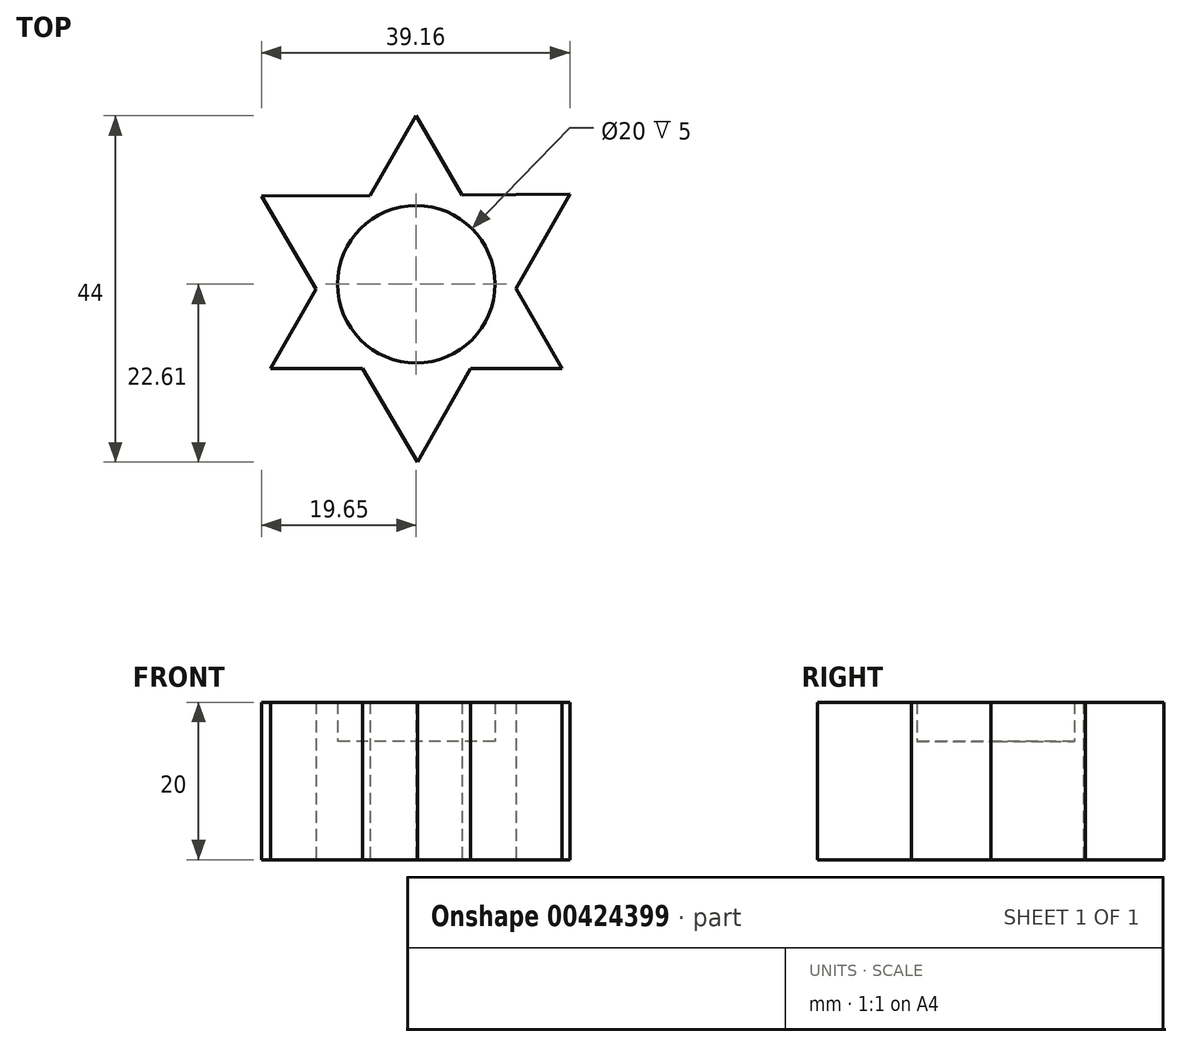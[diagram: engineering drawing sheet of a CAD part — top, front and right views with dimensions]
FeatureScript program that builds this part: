
annotation { "Feature Type Name" : "Feature", "Feature Type Description" : "" }
export const myFeature = defineFeature(function(context is Context, id is Id, definition is map)
    precondition{}
    {
        {
            var Q0;
            Q0=qCreatedBy(makeId("Top.planeOp"),FACE);
            var sketch = newSketch(context, id + "F0", { "sketchPlane" : qUnion([Q0])});
            skCircle(sketch, "E0.cCircle", {"center": v(0, 0) * mm, "radius": 21.4 * mm, "construction": true});
            skLineSegment(sketch, "E0.0", {"start": v(0, 21.4) * mm, "end": v(18.53, -10.7) * mm});
            skLineSegment(sketch, "E0.1", {"start": v(18.53, -10.7) * mm, "end": v(-18.53, -10.7) * mm});
            skLineSegment(sketch, "E0.2", {"start": v(-18.53, -10.7) * mm, "end": v(0, 21.4) * mm});
            skCircle(sketch, "E1.cCircle", {"center": v(0, 0) * mm, "radius": 22.6 * mm, "construction": true});
            skLineSegment(sketch, "E1.0", {"start": v(19.5, 11.42) * mm, "end": v(0.14, -22.6) * mm});
            skLineSegment(sketch, "E1.1", {"start": v(0.14, -22.6) * mm, "end": v(-19.65, 11.18) * mm});
            skLineSegment(sketch, "E1.2", {"start": v(-19.65, 11.18) * mm, "end": v(19.5, 11.42) * mm});
            skLineSegment(sketch, "E2", {"start": v(0, 21.4) * mm, "end": v(0.14, -22.6) * mm});
            skSolve(sketch);
        }
        {
            var Q0;
            {var subQ0=sQuery(id+"F0.wireOp",EDGE,"E1.1");var subQ1=sQuery(id+"F0.wireOp",EDGE,"E0.2");var subQ2=makeQuery(id+"F0.imprint","INTERSECT",VERTEX,{"derivedFrom":[subQ1,subQ0]});Q0=makeQuery(id+"F0.imprint","IMPRINT",FACE,{"disambiguationData":[TD([[makeQuery(id+"F0.imprint","IMPRINT",EDGE,{"disambiguationData":[TD([[subQ2,-1.0]])],"derivedFrom":subQ1}),1.0]])]});}
            var Q1;
            {var subQ5=sQuery(id+"F0.wireOp",EDGE,"E1.1");var subQ6=sQuery(id+"F0.wireOp",EDGE,"E0.1");var subQ7=makeQuery(id+"F0.imprint","INTERSECT",VERTEX,{"derivedFrom":[subQ6,subQ5]});Q1=makeQuery(id+"F0.imprint","IMPRINT",FACE,{"disambiguationData":[TD([[makeQuery(id+"F0.imprint","IMPRINT",EDGE,{"disambiguationData":[TD([[subQ7,1.0]])],"derivedFrom":subQ6}),-1.0]])]});}
            var Q2;
            {var subQ1=sQuery(id+"F0.wireOp",EDGE,"E0.2");var subQ3=sQuery(id+"F0.wireOp",EDGE,"E1.2");var subQ4=makeQuery(id+"F0.imprint","INTERSECT",VERTEX,{"derivedFrom":[subQ1,subQ3]});Q2=makeQuery(id+"F0.imprint","IMPRINT",FACE,{"disambiguationData":[TD([[makeQuery(id+"F0.imprint","IMPRINT",EDGE,{"disambiguationData":[TD([[subQ4,-1.0]])],"derivedFrom":subQ3}),1.0]])]});}
            var Q3;
            {var subQ1=sQuery(id+"F0.wireOp",EDGE,"E0.0");var subQ3=sQuery(id+"F0.wireOp",EDGE,"E1.2");var subQ4=makeQuery(id+"F0.imprint","INTERSECT",VERTEX,{"derivedFrom":[subQ1,subQ3]});Q3=makeQuery(id+"F0.imprint","IMPRINT",FACE,{"disambiguationData":[TD([[makeQuery(id+"F0.imprint","IMPRINT",EDGE,{"disambiguationData":[TD([[subQ4,1.0]])],"derivedFrom":subQ3}),1.0]])]});}
            var Q4;
            {var subQ0=sQuery(id+"F0.wireOp",EDGE,"E1.2");var subQ1=sQuery(id+"F0.wireOp",EDGE,"E0.0");var subQ2=makeQuery(id+"F0.imprint","INTERSECT",VERTEX,{"derivedFrom":[subQ1,subQ0]});Q4=makeQuery(id+"F0.imprint","IMPRINT",FACE,{"disambiguationData":[TD([[makeQuery(id+"F0.imprint","IMPRINT",EDGE,{"disambiguationData":[TD([[subQ2,-1.0]])],"derivedFrom":subQ1}),-1.0]])]});}
            var Q5;
            {var subQ0=sQuery(id+"F0.wireOp",EDGE,"E1.2");var subQ1=sQuery(id+"F0.wireOp",EDGE,"E0.0");var subQ2=makeQuery(id+"F0.imprint","INTERSECT",VERTEX,{"derivedFrom":[subQ1,subQ0]});Q5=makeQuery(id+"F0.imprint","IMPRINT",FACE,{"disambiguationData":[TD([[makeQuery(id+"F0.imprint","IMPRINT",EDGE,{"disambiguationData":[TD([[subQ2,-1.0]])],"derivedFrom":subQ1}),1.0]])]});}
            var Q6;
            {var subQ0=sQuery(id+"F0.wireOp",EDGE,"E0.1");var subQ1=sQuery(id+"F0.wireOp",EDGE,"E0.0");var subQ2=makeQuery(id+"F0.imprint","INTERSECT",VERTEX,{"derivedFrom":[subQ1,subQ0]});Q6=makeQuery(id+"F0.imprint","IMPRINT",FACE,{"disambiguationData":[TD([[makeQuery(id+"F0.imprint","IMPRINT",EDGE,{"disambiguationData":[TD([[subQ2,1.0]])],"derivedFrom":subQ1}),-1.0]])]});}
            var Q7;
            {var subQ0=sQuery(id+"F0.wireOp",EDGE,"E1.1");var subQ1=sQuery(id+"F0.wireOp",EDGE,"E0.1");var subQ2=makeQuery(id+"F0.imprint","INTERSECT",VERTEX,{"derivedFrom":[subQ1,subQ0]});Q7=makeQuery(id+"F0.imprint","IMPRINT",FACE,{"disambiguationData":[TD([[makeQuery(id+"F0.imprint","IMPRINT",EDGE,{"disambiguationData":[TD([[subQ2,1.0]])],"derivedFrom":subQ1}),1.0]])]});}
            var Q8;
            {var subQ0=sQuery(id+"F0.wireOp",EDGE,"E1.0");var subQ1=sQuery(id+"F0.wireOp",EDGE,"E0.1");var subQ2=makeQuery(id+"F0.imprint","INTERSECT",VERTEX,{"derivedFrom":[subQ1,subQ0]});Q8=makeQuery(id+"F0.imprint","IMPRINT",FACE,{"disambiguationData":[TD([[makeQuery(id+"F0.imprint","IMPRINT",EDGE,{"disambiguationData":[TD([[subQ2,-1.0]])],"derivedFrom":subQ1}),1.0]])]});}
            var Q9;
            {var subQ0=sQuery(id+"F0.wireOp",EDGE,"E0.2");var subQ1=sQuery(id+"F0.wireOp",EDGE,"E0.1");var subQ2=makeQuery(id+"F0.imprint","INTERSECT",VERTEX,{"derivedFrom":[subQ1,subQ0]});Q9=makeQuery(id+"F0.imprint","IMPRINT",FACE,{"disambiguationData":[TD([[makeQuery(id+"F0.imprint","IMPRINT",EDGE,{"disambiguationData":[TD([[subQ2,1.0]])],"derivedFrom":subQ1}),-1.0]])]});}
            extrude(context, id + "F1", {"entities" : qUnion([Q0, Q1, Q2, Q3, Q4, Q5, Q6, Q7, Q8, Q9]), "depth" : 15 * mm, "offsetDistance" : 25 * mm});
        }
        {
            var Q0;
            Q0=makeQuery(id+"F1.opExtrude","CAP_FACE",FACE,{"disambiguationData":[OSD([sQuery(id+"F0.wireOp",EDGE,"E0.0"),sQuery(id+"F0.wireOp",EDGE,"E0.1"),sQuery(id+"F0.wireOp",EDGE,"E0.2"),sQuery(id+"F0.wireOp",EDGE,"E1.0"),sQuery(id+"F0.wireOp",EDGE,"E1.1"),sQuery(id+"F0.wireOp",EDGE,"E1.2")])],"isStart":false});
            var sketch = newSketch(context, id + "F2", { "sketchPlane" : qUnion([Q0])});
            skCircle(sketch, "E3", {"center": v(0, 0) * mm, "radius": 10 * mm});
            skLineSegment(sketch, "E4", {"start": v(0, 0) * mm, "end": v(10, 0) * mm});
            skSolve(sketch);
        }
        {
            var Q0;
            Q0=makeQuery(id+"F2.imprint","IMPRINT",FACE,{"disambiguationData":[TD([[makeQuery(id+"F2.imprint","IMPRINT",EDGE,{"derivedFrom":sQuery(id+"F2.wireOp",EDGE,"E3")}),-1.0]])]});
            extrude(context, id + "F3", {"entities" : qUnion([Q0]), "operationType" : NewBodyOperationType.ADD, "depth" : 5 * mm, "offsetDistance" : 25 * mm});
        }
    });
